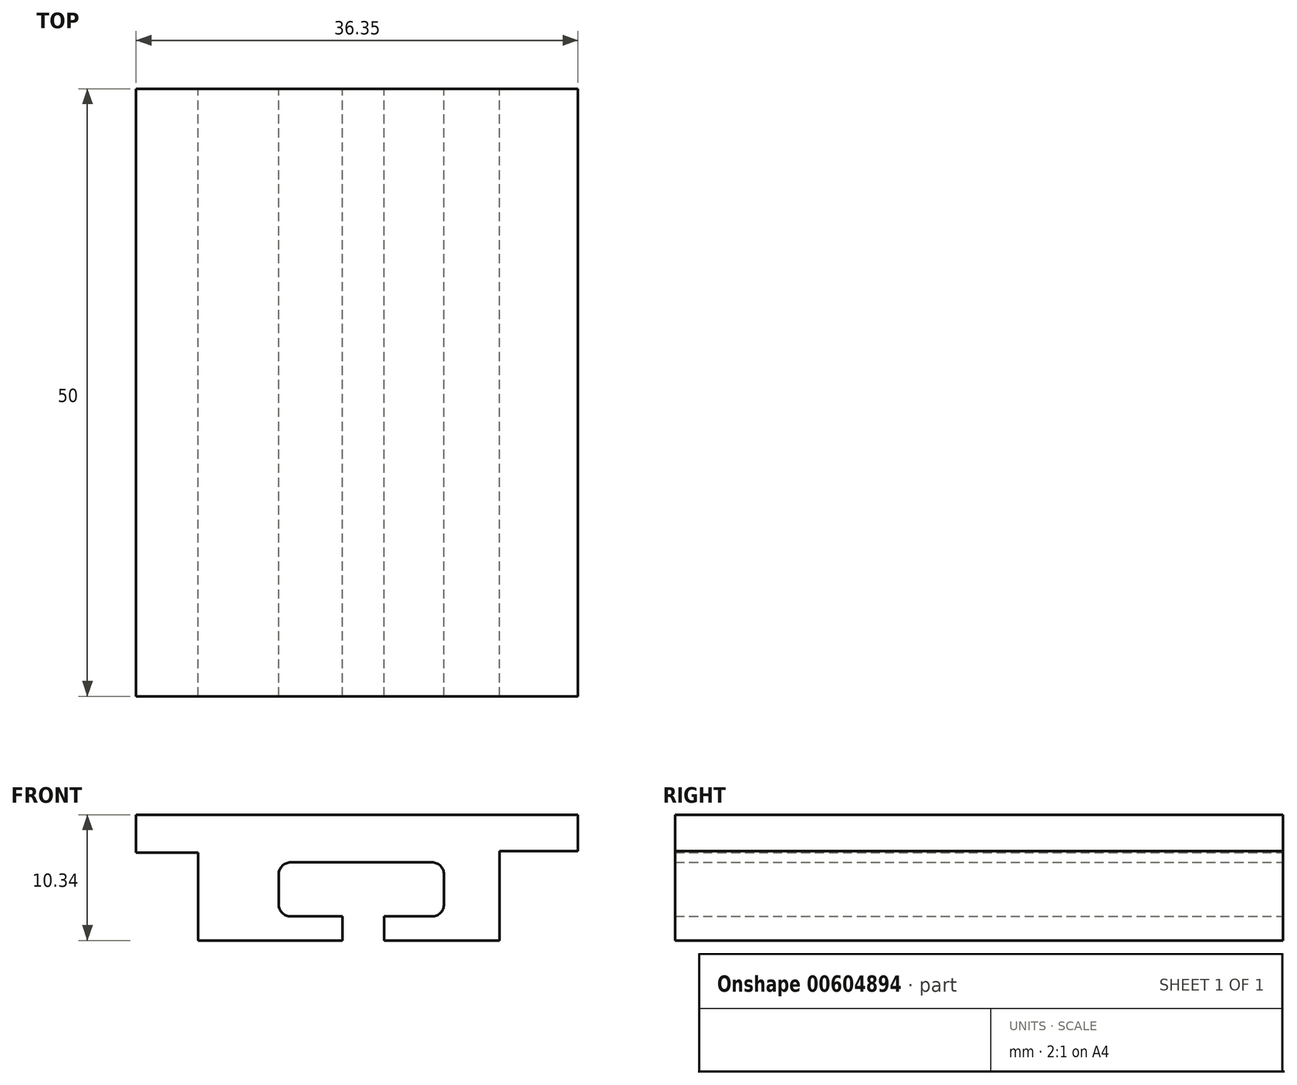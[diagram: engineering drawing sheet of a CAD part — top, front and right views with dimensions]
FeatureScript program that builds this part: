
annotation { "Feature Type Name" : "Feature", "Feature Type Description" : "" }
export const myFeature = defineFeature(function(context is Context, id is Id, definition is map)
    precondition{}
    {
        {
            var Q0;
            Q0=qCreatedBy(makeId("Front.planeOp"),FACE);
            var sketch = newSketch(context, id + "F0", { "sketchPlane" : qUnion([Q0])});
            skLineSegment(sketch, "E0.bottom", {"start": v(0, 0) * mm, "end": v(-36.35, 0) * mm});
            skLineSegment(sketch, "E0.top", {"start": v(0, 10.34) * mm, "end": v(-36.35, 10.34) * mm});
            skLineSegment(sketch, "E0.left", {"start": v(0, 0) * mm, "end": v(0, 10.34) * mm});
            skLineSegment(sketch, "E0.right", {"start": v(-36.35, 0) * mm, "end": v(-36.35, 10.34) * mm});
            skLineSegment(sketch, "E1.bottom", {"start": v(-24.26, 0) * mm, "end": v(-11.22, 0) * mm});
            skLineSegment(sketch, "E2", {"start": v(-31.26, 0) * mm, "end": v(-31.26, 10.34) * mm});
            skLineSegment(sketch, "E3", {"start": v(-6.44, 10.34) * mm, "end": v(-6.44, 0) * mm});
            skLineSegment(sketch, "E4", {"start": v(-36.35, 7.22) * mm, "end": v(-31.26, 7.22) * mm});
            skLineSegment(sketch, "E5", {"start": v(-6.44, 7.36) * mm, "end": v(0, 7.36) * mm});
            skPoint(sketch, "E5.endSnap0", {"position": v(0, 5.17) * mm});
            skLineSegment(sketch, "E6.bottom", {"start": v(-24.62, 6.43) * mm, "end": v(-11.02, 6.43) * mm});
            skLineSegment(sketch, "E6.top", {"start": v(-24.62, 1.97) * mm, "end": v(-11.02, 1.97) * mm});
            skLineSegment(sketch, "E6.left", {"start": v(-24.62, 6.43) * mm, "end": v(-24.62, 1.97) * mm});
            skLineSegment(sketch, "E6.right", {"start": v(-11.02, 6.43) * mm, "end": v(-11.02, 1.97) * mm});
            skLineSegment(sketch, "E7", {"start": v(-19.37, 1.97) * mm, "end": v(-19.37, 0) * mm});
            skLineSegment(sketch, "E8", {"start": v(-15.95, 1.97) * mm, "end": v(-15.95, 0) * mm});
            skSolve(sketch);
        }
        {
            var Q0;
            Q0=makeQuery(id+"F0.imprint","IMPRINT",FACE,{"disambiguationData":[TD([[makeQuery(id+"F0.imprint","IMPRINT",EDGE,{"derivedFrom":sQuery(id+"F0.wireOp",EDGE,"E6.bottom")}),1.0]])]});
            var Q1;
            {var subQ5=sQuery(id+"F0.wireOp",EDGE,"E5");Q1=makeQuery(id+"F0.imprint","IMPRINT",FACE,{"disambiguationData":[TD([[makeQuery(id+"F0.imprint","IMPRINT",EDGE,{"derivedFrom":subQ5}),1.0]])]});}
            var Q2;
            {var subQ5=sQuery(id+"F0.wireOp",EDGE,"E4");Q2=makeQuery(id+"F0.imprint","IMPRINT",FACE,{"disambiguationData":[TD([[makeQuery(id+"F0.imprint","IMPRINT",EDGE,{"derivedFrom":subQ5}),1.0]])]});}
            extrude(context, id + "F1", {"entities" : qUnion([Q0, Q1, Q2]), "depth" : 50 * mm, "offsetDistance" : 25 * mm});
        }
        {
            var Q0;
            Q0=makeQuery(id+"F1.opExtrude","SWEPT_EDGE",EDGE,{"disambiguationData":[OSD([sQuery(id+"F0.wireOp",EDGE,"E6.bottom"),sQuery(id+"F0.wireOp",EDGE,"E6.left")])]});
            var Q1;
            Q1=makeQuery(id+"F1.opExtrude","SWEPT_EDGE",EDGE,{"disambiguationData":[OSD([sQuery(id+"F0.wireOp",EDGE,"E6.bottom"),sQuery(id+"F0.wireOp",EDGE,"E6.right")])]});
            var Q2;
            Q2=makeQuery(id+"F1.opExtrude","SWEPT_EDGE",EDGE,{"disambiguationData":[OSD([sQuery(id+"F0.wireOp",EDGE,"E6.top"),sQuery(id+"F0.wireOp",EDGE,"E6.right")])]});
            var Q3;
            Q3=makeQuery(id+"F1.opExtrude","SWEPT_EDGE",EDGE,{"disambiguationData":[OSD([sQuery(id+"F0.wireOp",EDGE,"E6.top"),sQuery(id+"F0.wireOp",EDGE,"E6.left")])]});
            fillet(context, id + "F2", {"entities" : qUnion([Q0, Q1, Q2, Q3]), "radius" : 1 * mm, "tangentPropagation" : true, "allowEdgeOverflow" : false});
        }
    });
